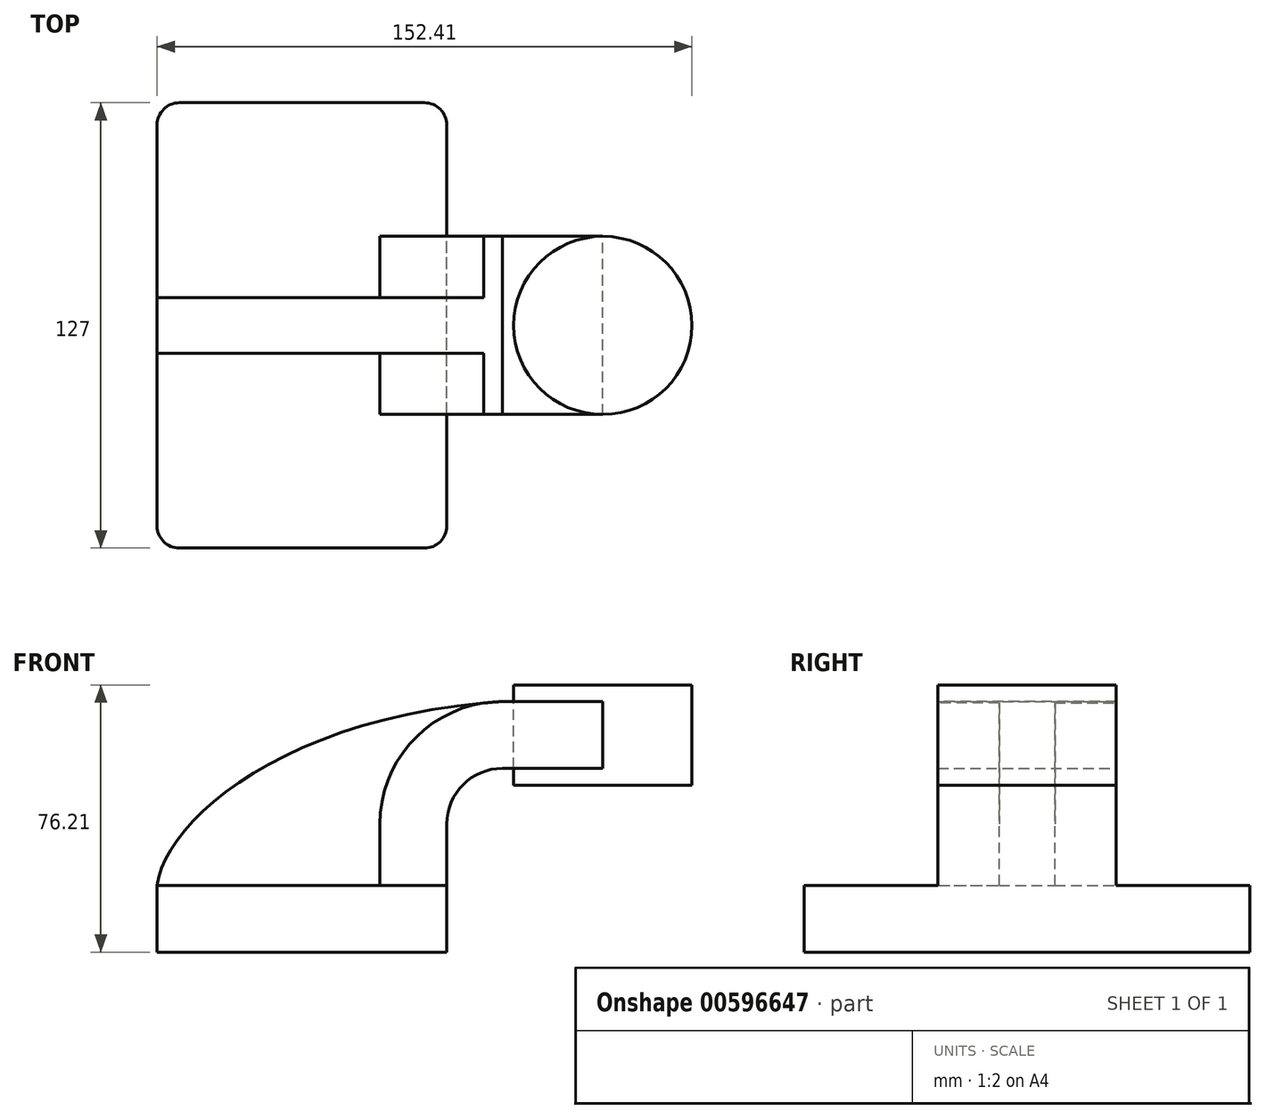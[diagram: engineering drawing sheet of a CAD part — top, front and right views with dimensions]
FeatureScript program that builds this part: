
annotation { "Feature Type Name" : "Feature", "Feature Type Description" : "" }
export const myFeature = defineFeature(function(context is Context, id is Id, definition is map)
    precondition{}
    {
        {
            var Q0;
            Q0=qCreatedBy(makeId("Front.planeOp"),FACE);
            var sketch = newSketch(context, id + "F0", { "sketchPlane" : qUnion([Q0])});
            skLineSegment(sketch, "E0.bottom", {"start": v(41.28, 9.53) * mm, "end": v(-41.28, 9.53) * mm});
            skLineSegment(sketch, "E0.top", {"start": v(41.28, -9.52) * mm, "end": v(-41.28, -9.52) * mm});
            skLineSegment(sketch, "E0.left", {"start": v(41.28, 9.53) * mm, "end": v(41.28, -9.52) * mm});
            skLineSegment(sketch, "E0.right", {"start": v(-41.28, 9.53) * mm, "end": v(-41.28, -9.52) * mm});
            skPoint(sketch, "E0.middle", {"position": v(0, 0) * mm});
            skLineSegment(sketch, "E1.bottom", {"start": v(111.12, 38.1) * mm, "end": v(60.32, 38.1) * mm});
            skLineSegment(sketch, "E1.top", {"start": v(111.12, 66.68) * mm, "end": v(60.32, 66.68) * mm});
            skLineSegment(sketch, "E1.left", {"start": v(111.12, 38.1) * mm, "end": v(111.12, 66.68) * mm});
            skLineSegment(sketch, "E1.right", {"start": v(60.32, 38.1) * mm, "end": v(60.32, 66.68) * mm});
            skPoint(sketch, "E1.middle", {"position": v(85.72, 52.39) * mm});
            skLineSegment(sketch, "E2", {"start": v(41.28, 9.53) * mm, "end": v(41.28, 27) * mm});
            skArc(sketch, "E3", {"start": v(41.27, 27) * mm, "mid": v(45.92, 38.23) * mm, "end": v(57.15, 42.88) * mm});
            skLineSegment(sketch, "E4", {"start": v(57.15, 42.88) * mm, "end": v(85.72, 42.88) * mm});
            skLineSegment(sketch, "E5.0", {"start": v(57.15, 61.93) * mm, "end": v(85.72, 61.93) * mm});
            skArc(sketch, "E5.1", {"start": v(22.22, 27) * mm, "mid": v(32.45, 51.7) * mm, "end": v(57.15, 61.93) * mm});
            skLineSegment(sketch, "E5.2", {"start": v(22.22, 9.53) * mm, "end": v(22.22, 27) * mm});
            skLineSegment(sketch, "E6", {"start": v(85.72, 66.68) * mm, "end": v(85.72, 38.1) * mm});
            skFitSpline(sketch, "E7", {"points": [v(-41.28, 9.52) * mm, v(57.15, 61.93) * mm], "startDerivative": vector(7.08, 54.81) * mm, "endDerivative": vector(186.59, 12.07) * mm});
            skSolve(sketch);
        }
        {
            var Q0;
            Q0=makeQuery(id+"F0.imprint","IMPRINT",FACE,{"disambiguationData":[TD([[makeQuery(id+"F0.imprint","IMPRINT",EDGE,{"derivedFrom":sQuery(id+"F0.wireOp",EDGE,"E0.top")}),-1.0]])]});
            extrude(context, id + "F1", {"entities" : qUnion([Q0]), "endBound" : BoundingType.SYMMETRIC, "depth" : 127 * mm, "offsetDistance" : 25.4 * mm});
        }
        {
            var Q0;
            {var subQ1=sQuery(id+"F0.wireOp",EDGE,"E2");Q0=makeQuery(id+"F0.imprint","IMPRINT",FACE,{"disambiguationData":[TD([[makeQuery(id+"F0.imprint","IMPRINT",EDGE,{"derivedFrom":subQ1}),1.0]])]});}
            var Q1;
            {var subQ0=sQuery(id+"F0.wireOp",EDGE,"E4");var subQ1=sQuery(id+"F0.wireOp",EDGE,"E1.right");var subQ2=makeQuery(id+"F0.imprint","INTERSECT",VERTEX,{"derivedFrom":[subQ1,subQ0]});Q1=makeQuery(id+"F0.imprint","IMPRINT",FACE,{"disambiguationData":[TD([[makeQuery(id+"F0.imprint","IMPRINT",EDGE,{"disambiguationData":[TD([[subQ2,-1.0]])],"derivedFrom":subQ1}),-1.0]])]});}
            extrude(context, id + "F2", {"entities" : qUnion([Q0, Q1]), "operationType" : NewBodyOperationType.ADD, "endBound" : BoundingType.SYMMETRIC, "depth" : 50.8 * mm, "offsetDistance" : 25.4 * mm});
        }
        {
            var Q0;
            {var subQ3=sQuery(id+"F0.wireOp",EDGE,"E5.2");Q0=makeQuery(id+"F0.imprint","IMPRINT",FACE,{"disambiguationData":[TD([[makeQuery(id+"F0.imprint","IMPRINT",EDGE,{"derivedFrom":subQ3}),1.0]])]});}
            extrude(context, id + "F3", {"entities" : qUnion([Q0]), "operationType" : NewBodyOperationType.ADD, "endBound" : BoundingType.SYMMETRIC, "depth" : 15.88 * mm, "offsetDistance" : 25.4 * mm});
        }
        {
            var Q0;
            {var subQ0=sQuery(id+"F0.wireOp",EDGE,"E1.left");Q0=makeQuery(id+"F0.imprint","IMPRINT",FACE,{"disambiguationData":[TD([[makeQuery(id+"F0.imprint","IMPRINT",EDGE,{"derivedFrom":subQ0}),1.0]])]});}
            var Q1;
            Q1=sQuery(id+"F0.wireOp",EDGE,"E6");
            revolve(context, id + "F4", {"entities" : qUnion([Q0]), "axis" : qUnion([Q1]), "revolveType" : RevolveType.FULL});
        }
        {
            var Q0;
            Q0=makeQuery(id+"F1.opExtrude","CAP_EDGE",EDGE,{"disambiguationData":[OSD([sQuery(id+"F0.wireOp",EDGE,"E0.left")])],"isStart":false});
            var Q1;
            Q1=makeQuery(id+"F1.opExtrude","CAP_EDGE",EDGE,{"disambiguationData":[OSD([sQuery(id+"F0.wireOp",EDGE,"E0.right")])],"isStart":false});
            var Q2;
            Q2=makeQuery(id+"F1.opExtrude","CAP_EDGE",EDGE,{"disambiguationData":[OSD([sQuery(id+"F0.wireOp",EDGE,"E0.left")])],"isStart":true});
            var Q3;
            Q3=makeQuery(id+"F1.opExtrude","CAP_EDGE",EDGE,{"disambiguationData":[OSD([sQuery(id+"F0.wireOp",EDGE,"E0.right")])],"isStart":true});
            fillet(context, id + "F5", {"entities" : qUnion([Q0, Q1, Q2, Q3]), "radius" : 6.35 * mm, "tangentPropagation" : true, "allowEdgeOverflow" : false});
        }
    });
